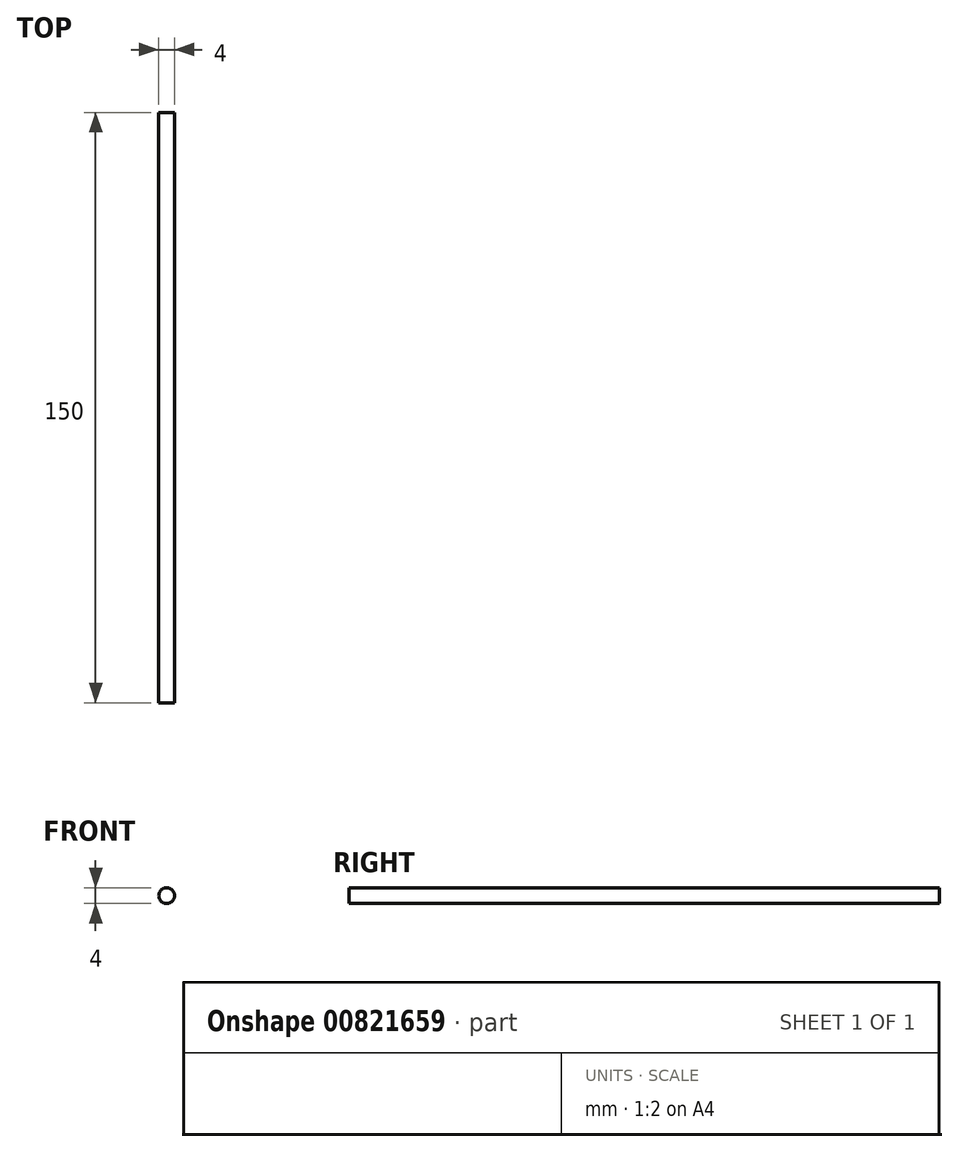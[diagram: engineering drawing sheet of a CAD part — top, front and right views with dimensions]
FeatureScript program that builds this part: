
annotation { "Feature Type Name" : "Feature", "Feature Type Description" : "" }
export const myFeature = defineFeature(function(context is Context, id is Id, definition is map)
    precondition{}
    {
        {
            var Q0;
            Q0=qCreatedBy(makeId("Front.planeOp"),FACE);
            var sketch = newSketch(context, id + "F0", { "sketchPlane" : qUnion([Q0])});
            skCircle(sketch, "E0", {"center": v(0, 0) * mm, "radius": 2 * mm});
            skSolve(sketch);
        }
        {
            var Q0;
            Q0 = qSketchRegion(id + "F0", true);
            extrude(context, id + "F1", {"entities" : qUnion([Q0]), "depth" : 150 * mm, "offsetDistance" : 25 * mm});
        }
    });
